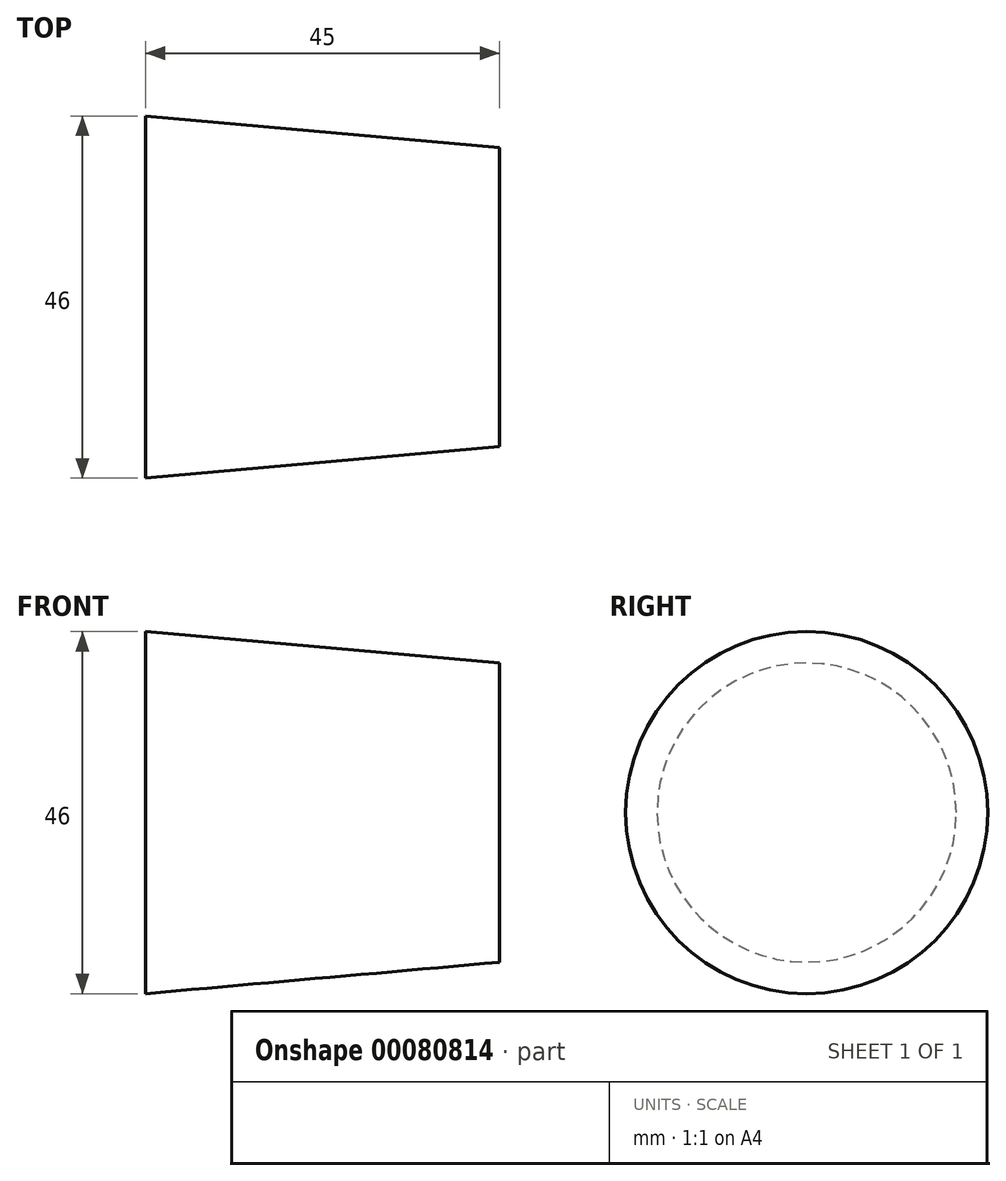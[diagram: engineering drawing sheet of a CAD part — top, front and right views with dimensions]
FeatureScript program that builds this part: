
annotation { "Feature Type Name" : "Feature", "Feature Type Description" : "" }
export const myFeature = defineFeature(function(context is Context, id is Id, definition is map)
    precondition{}
    {
        {
            var Q0;
            Q0=qCreatedBy(makeId("Top.planeOp"),FACE);
            var sketch = newSketch(context, id + "F0", { "sketchPlane" : qUnion([Q0])});
            skLineSegment(sketch, "E0", {"start": v(0, 0) * mm, "end": v(-45, 0) * mm});
            skLineSegment(sketch, "E1", {"start": v(-45, 0) * mm, "end": v(-45, 23) * mm});
            skLineSegment(sketch, "E2", {"start": v(0, 0) * mm, "end": v(0, 19) * mm});
            skLineSegment(sketch, "E3", {"start": v(-45, 23) * mm, "end": v(0, 19) * mm});
            skSolve(sketch);
        }
        {
            var Q0;
            Q0=sQuery(id+"F0.wireOp",EDGE,"E1");
            var Q1;
            Q1=sQuery(id+"F0.wireOp",EDGE,"E3");
            var Q2;
            Q2=sQuery(id+"F0.wireOp",EDGE,"E2");
            var Q3;
            Q3=sQuery(id+"F0.wireOp",EDGE,"E0");
            revolve(context, id + "F1", {"bodyType" : ToolBodyType.SURFACE, "operationType" : NewBodyOperationType.REMOVE, "surfaceEntities" : qUnion([Q0, Q1, Q2]), "axis" : qUnion([Q3]), "revolveType" : RevolveType.FULL, "oppositeDirection" : true});
        }
    });
